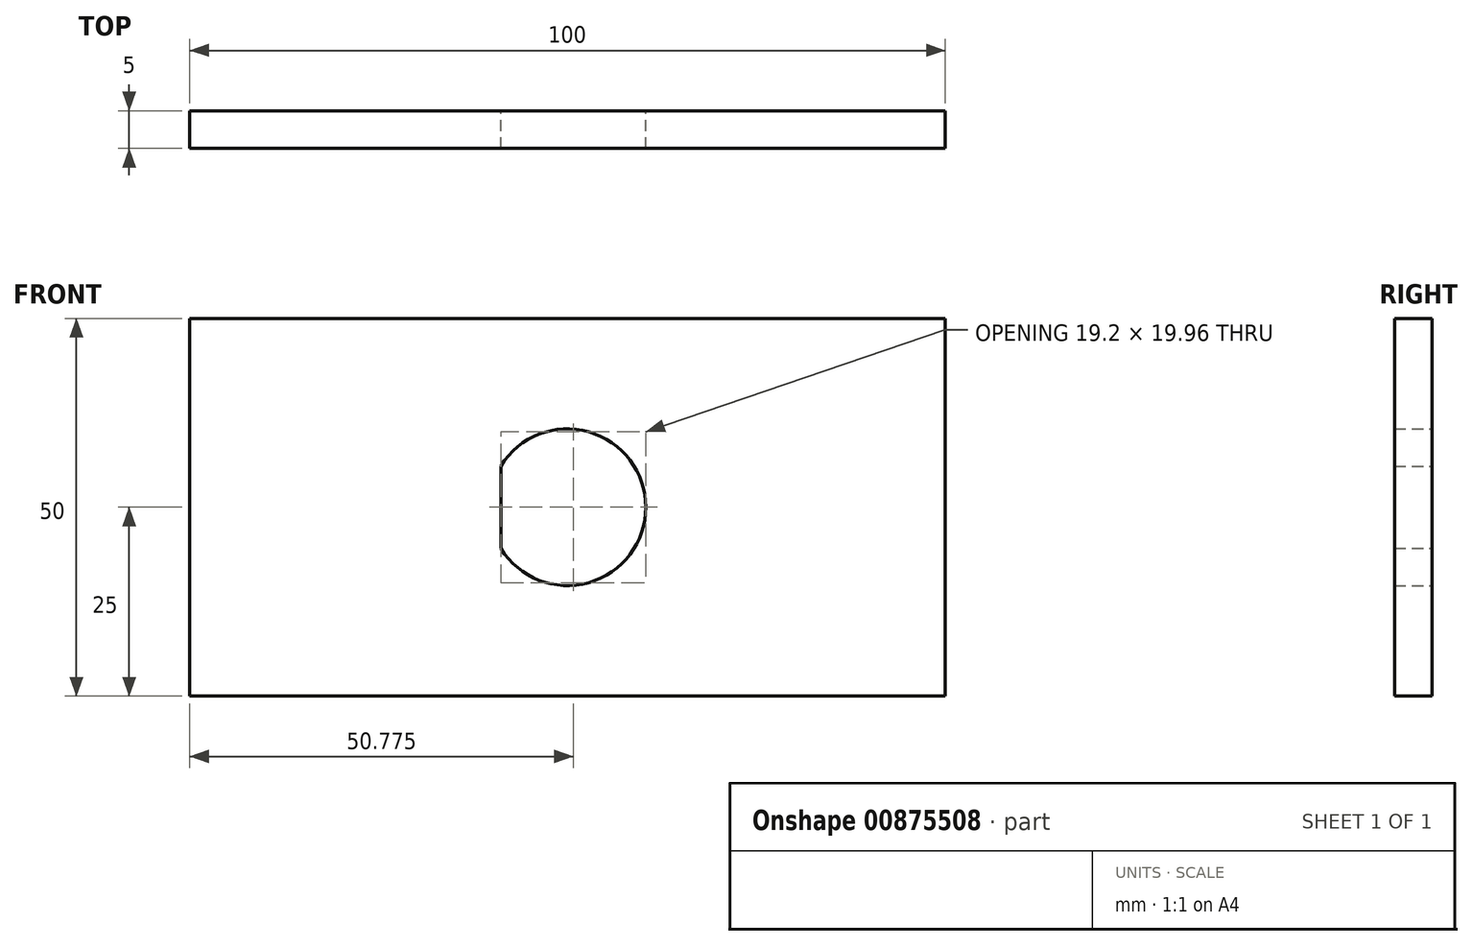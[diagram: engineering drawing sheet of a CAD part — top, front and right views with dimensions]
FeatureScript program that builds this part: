
annotation { "Feature Type Name" : "Feature", "Feature Type Description" : "" }
export const myFeature = defineFeature(function(context is Context, id is Id, definition is map)
    precondition{}
    {
        {
            var Q0;
            Q0=qCreatedBy(makeId("Front.planeOp"),FACE);
            var sketch = newSketch(context, id + "F0", { "sketchPlane" : qUnion([Q0])});
            skLineSegment(sketch, "E0.bottom", {"start": v(50, 25) * mm, "end": v(-50, 25) * mm});
            skLineSegment(sketch, "E0.top", {"start": v(50, -25) * mm, "end": v(-50, -25) * mm});
            skLineSegment(sketch, "E0.left", {"start": v(50, 25) * mm, "end": v(50, -25) * mm});
            skLineSegment(sketch, "E0.right", {"start": v(-50, 25) * mm, "end": v(-50, -25) * mm});
            skPoint(sketch, "E0.middle", {"position": v(0, 0) * mm});
            skArc(sketch, "E1", {"start": v(-8.83, -5.46) * mm, "mid": v(10.38, 0) * mm, "end": v(-8.83, 5.46) * mm});
            skLineSegment(sketch, "E2", {"start": v(-8.83, 5.46) * mm, "end": v(-8.83, -5.46) * mm});
            skLineSegment(sketch, "E3", {"start": v(-8.83, 0) * mm, "end": v(10.38, 0) * mm});
            skPoint(sketch, "E4", {"position": v(10.38, 0) * mm});
            skSolve(sketch);
        }
        {
            var Q0;
            Q0=makeQuery(id+"F0.imprint","IMPRINT",FACE,{"disambiguationData":[TD([[makeQuery(id+"F0.imprint","IMPRINT",EDGE,{"derivedFrom":sQuery(id+"F0.wireOp",EDGE,"E0.bottom")}),1.0]])]});
            extrude(context, id + "F1", {"entities" : qUnion([Q0]), "endBound" : BoundingType.SYMMETRIC, "depth" : 5 * mm, "offsetDistance" : 25 * mm});
        }
    });
